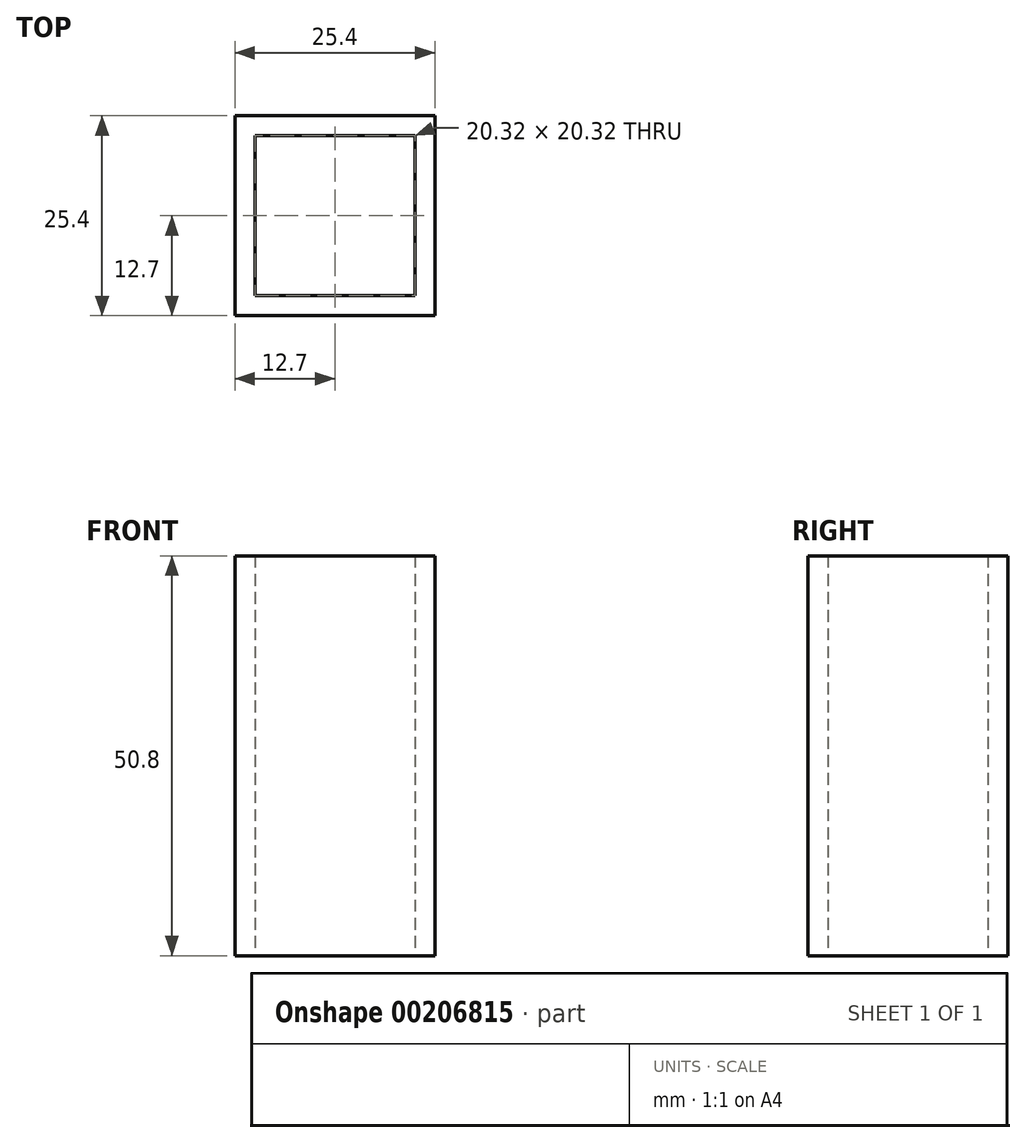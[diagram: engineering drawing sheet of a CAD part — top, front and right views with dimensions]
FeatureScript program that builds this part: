
annotation { "Feature Type Name" : "Feature", "Feature Type Description" : "" }
export const myFeature = defineFeature(function(context is Context, id is Id, definition is map)
    precondition{}
    {
        {
            var Q0;
            Q0=qCreatedBy(makeId("Top.planeOp"),FACE);
            var sketch = newSketch(context, id + "F0", { "sketchPlane" : qUnion([Q0])});
            skLineSegment(sketch, "E0.bottom", {"start": v(12.7, -12.7) * mm, "end": v(-12.7, -12.7) * mm});
            skLineSegment(sketch, "E0.top", {"start": v(12.7, 12.7) * mm, "end": v(-12.7, 12.7) * mm});
            skLineSegment(sketch, "E0.left", {"start": v(12.7, -12.7) * mm, "end": v(12.7, 12.7) * mm});
            skLineSegment(sketch, "E0.right", {"start": v(-12.7, -12.7) * mm, "end": v(-12.7, 12.7) * mm});
            skPoint(sketch, "E0.middle", {"position": v(0, 0) * mm});
            skLineSegment(sketch, "E1.0", {"start": v(10.16, 10.16) * mm, "end": v(-10.16, 10.16) * mm});
            skLineSegment(sketch, "E1.1", {"start": v(10.16, -10.16) * mm, "end": v(10.16, 10.16) * mm});
            skLineSegment(sketch, "E1.2", {"start": v(10.16, -10.16) * mm, "end": v(-10.16, -10.16) * mm});
            skLineSegment(sketch, "E1.3", {"start": v(-10.16, -10.16) * mm, "end": v(-10.16, 10.16) * mm});
            skSolve(sketch);
        }
        {
            var Q0;
            Q0=makeQuery(id+"F0.imprint","IMPRINT",FACE,{"disambiguationData":[TD([[makeQuery(id+"F0.imprint","IMPRINT",EDGE,{"derivedFrom":sQuery(id+"F0.wireOp",EDGE,"E0.bottom")}),-1.0]])]});
            extrude(context, id + "F1", {"entities" : qUnion([Q0]), "depth" : 50.8 * mm});
        }
    });
